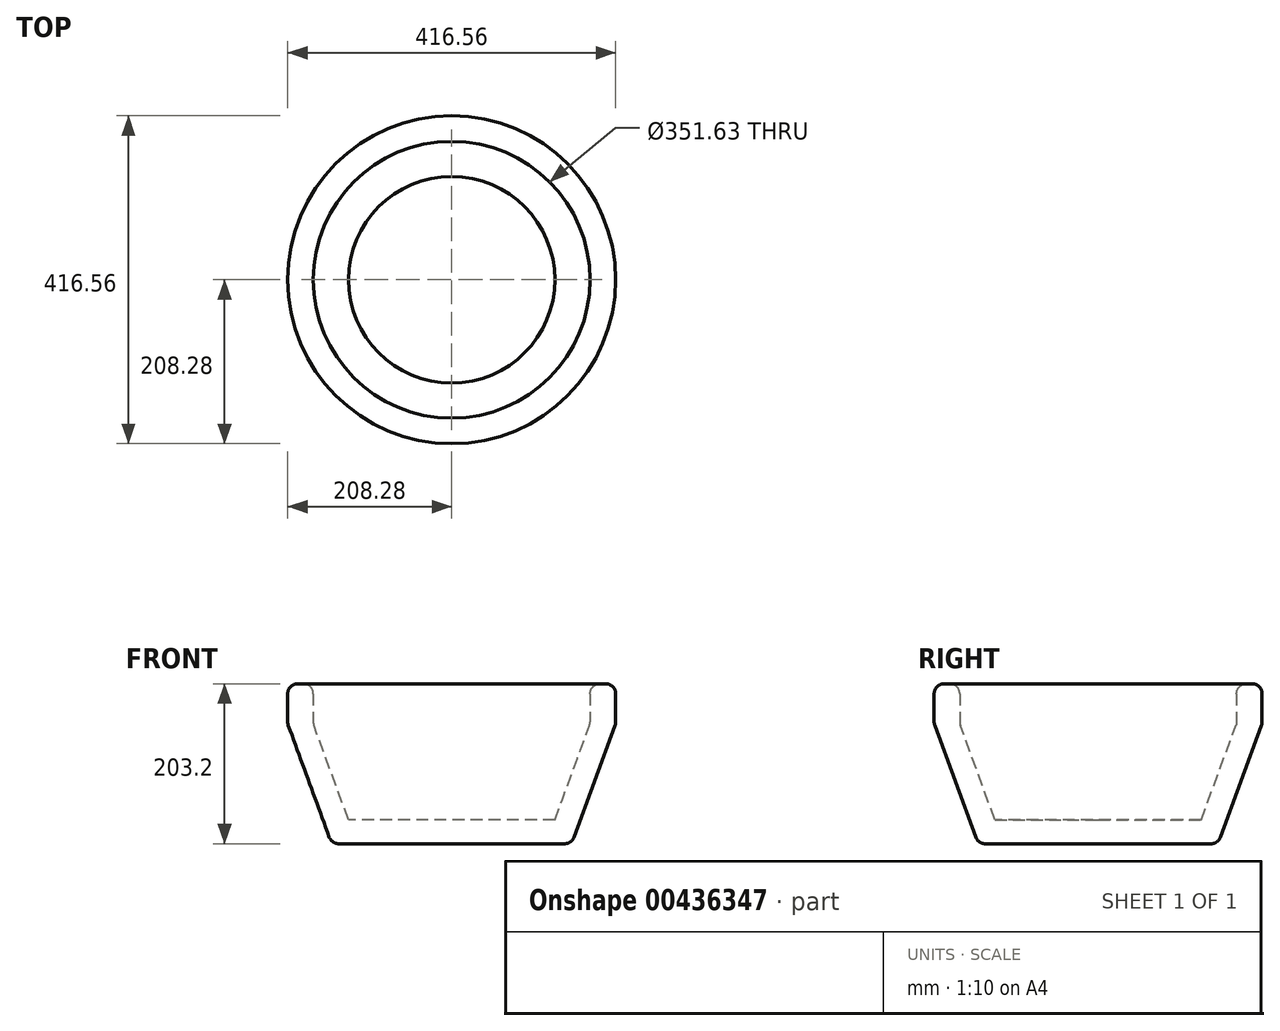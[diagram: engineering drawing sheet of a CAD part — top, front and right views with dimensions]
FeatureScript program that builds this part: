
annotation { "Feature Type Name" : "Feature", "Feature Type Description" : "" }
export const myFeature = defineFeature(function(context is Context, id is Id, definition is map)
    precondition{}
    {
        {
            var Q0;
            Q0=qCreatedBy(makeId("Front.planeOp"),FACE);
            var sketch = newSketch(context, id + "F0", { "sketchPlane" : qUnion([Q0])});
            skLineSegment(sketch, "E0", {"start": v(0, 0) * mm, "end": v(-152.4, 0) * mm});
            skLineSegment(sketch, "E1", {"start": v(-152.4, 0) * mm, "end": v(-208.28, 152.4) * mm});
            skLineSegment(sketch, "E2", {"start": v(-208.28, 152.4) * mm, "end": v(0, 152.4) * mm});
            skLineSegment(sketch, "E3", {"start": v(0, 152.4) * mm, "end": v(0, 0) * mm});
            skSolve(sketch);
        }
        {
            var Q0;
            Q0=makeQuery(id+"F0.imprint","IMPRINT",FACE,{"disambiguationData":[TD([[makeQuery(id+"F0.imprint","IMPRINT",EDGE,{"derivedFrom":sQuery(id+"F0.wireOp",EDGE,"E0")}),-1.0]])]});
            var Q1;
            Q1=sQuery(id+"F0.wireOp",EDGE,"E3");
            revolve(context, id + "F1", {"entities" : qUnion([Q0]), "axis" : qUnion([Q1]), "revolveType" : RevolveType.FULL});
        }
        {
            var Q0;
            Q0=makeQuery(id+"F1.opRevolve","SWEPT_FACE",FACE,{"disambiguationData":[OSD([sQuery(id+"F0.wireOp",EDGE,"E2")])]});
            shell(context, id + "F2", {"entities" : qUnion([Q0]), "thickness" : 30.48 * mm});
        }
        {
            var Q0;
            Q0=makeQuery(id+"F1.opRevolve","SWEPT_FACE",FACE,{"disambiguationData":[OSD([sQuery(id+"F0.wireOp",EDGE,"E2")])]});
            extrude(context, id + "F3", {"entities" : qUnion([Q0]), "operationType" : NewBodyOperationType.ADD, "depth" : 50.8 * mm});
        }
        {
            var Q0;
            Q0=makeQuery(id+"F3.opExtrude","CAP_FACE",FACE,{"disambiguationData":[OSD([sQuery(id+"F0.wireOp",EDGE,"E2")])],"isStart":false});
            var Q1;
            {var subQ0=sQuery(id+"F0.wireOp",EDGE,"E2");var subQ1=sQuery(id+"F0.wireOp",EDGE,"E1");var subQ2=makeQuery(id+"F2.opShell","OFFSET_EDGE",EDGE,{"disambiguationData":[OSD([subQ1,subQ0])]});Q1=makeQuery(id+"F3.boolean.opBoolean","MERGE",EDGE,{"derivedFrom":[subQ2,makeQuery(id+"F3.opExtrude","CAP_EDGE",EDGE,{"disambiguationData":[OSD([subQ1,subQ0]),TDD([subQ2])],"isStart":true})]});}
            var Q2;
            {var subQ0=sQuery(id+"F0.wireOp",EDGE,"E2");var subQ1=sQuery(id+"F0.wireOp",EDGE,"E1");var subQ2=makeQuery(id+"F1.opRevolve","SWEPT_EDGE",EDGE,{"disambiguationData":[OSD([subQ1,subQ0])]});Q2=makeQuery(id+"F3.boolean.opBoolean","MERGE",EDGE,{"derivedFrom":[subQ2,makeQuery(id+"F3.opExtrude","CAP_EDGE",EDGE,{"disambiguationData":[OSD([subQ1,subQ0]),TDD([subQ2])],"isStart":true})]});}
            var Q3;
            Q3=makeQuery(id+"F1.opRevolve","SWEPT_FACE",FACE,{"disambiguationData":[OSD([sQuery(id+"F0.wireOp",EDGE,"E0")])]});
            fillet(context, id + "F4", {"entities" : qUnion([Q0, Q1, Q2, Q3]), "radius" : 12.7 * mm, "tangentPropagation" : true, "allowEdgeOverflow" : false});
        }
    });
